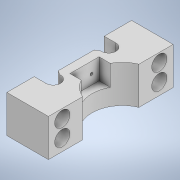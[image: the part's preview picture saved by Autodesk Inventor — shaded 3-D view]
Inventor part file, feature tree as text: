
AUTODESK INVENTOR PART (.ipt)
format: ipt  version: 2020 (Build 240168000, 168)  size: 209,920 bytes
history: native  units: mm
features: extrude x6, sketch x5, other x1
ambient origin geometry x8: Origin, YZ Plane, XZ Plane, XY Plane, X Axis, Y Axis, Z Axis, Center Point
bodies: Body1 (feature_tree)
feature tree (12):
  other  "Bryła1"
  extrude  "Wyciągnięcie proste1"  Depth=1.0mm
  sketch  "Szkic3"
  extrude  "Wyciągnięcie proste2"  Depth=20.0mm
  extrude  "Wyciągnięcie proste3"  Depth=90.0mm
  extrude  "Wyciągnięcie proste4"  Depth=45.0mm
  extrude  "Wyciągnięcie proste8"  Depth=30.0mm
  extrude  "Wyciągnięcie proste9"  Depth=27.0mm TaperAngle=0.0deg
  sketch  "Szkic2"
  sketch  "Szkic4"
  sketch  "Szkic8"
  sketch  "Szkic9"
